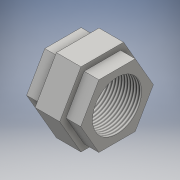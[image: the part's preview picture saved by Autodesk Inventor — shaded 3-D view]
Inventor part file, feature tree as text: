
AUTODESK INVENTOR PART (.ipt)
format: ipt  version: 2016 (Build 200138000, 138)  size: 121,344 bytes
history: native  units: mm
features: extrude x2, sketch x2, thread x1
ambient origin geometry x8: Origin, YZ Plane, XZ Plane, XY Plane, X Axis, Y Axis, Z Axis, Center Point
bodies: Solid1 (feature_tree)
feature tree (5):
  extrude  "Extrusion1"  Depth=64.0mm
  extrude  "Extrusion2"  Depth=10.0mm
  thread  "Thread1"  [1 undecoded]
  sketch  "Sketch1"  dims[d0=100.0mm d1=64.0mm]
  sketch  "Sketch3"  dims[d2=110.0mm d3=0.0mm d4=75.0mm d5=50.0mm d6=0.0mm d7=10.0mm d8=0.0mm]
note: 1 required parameter value undecoded (feature->parameter linkage not recoverable at this tier; creation-order binding heuristic only, values carry confidence <= 0.55)
